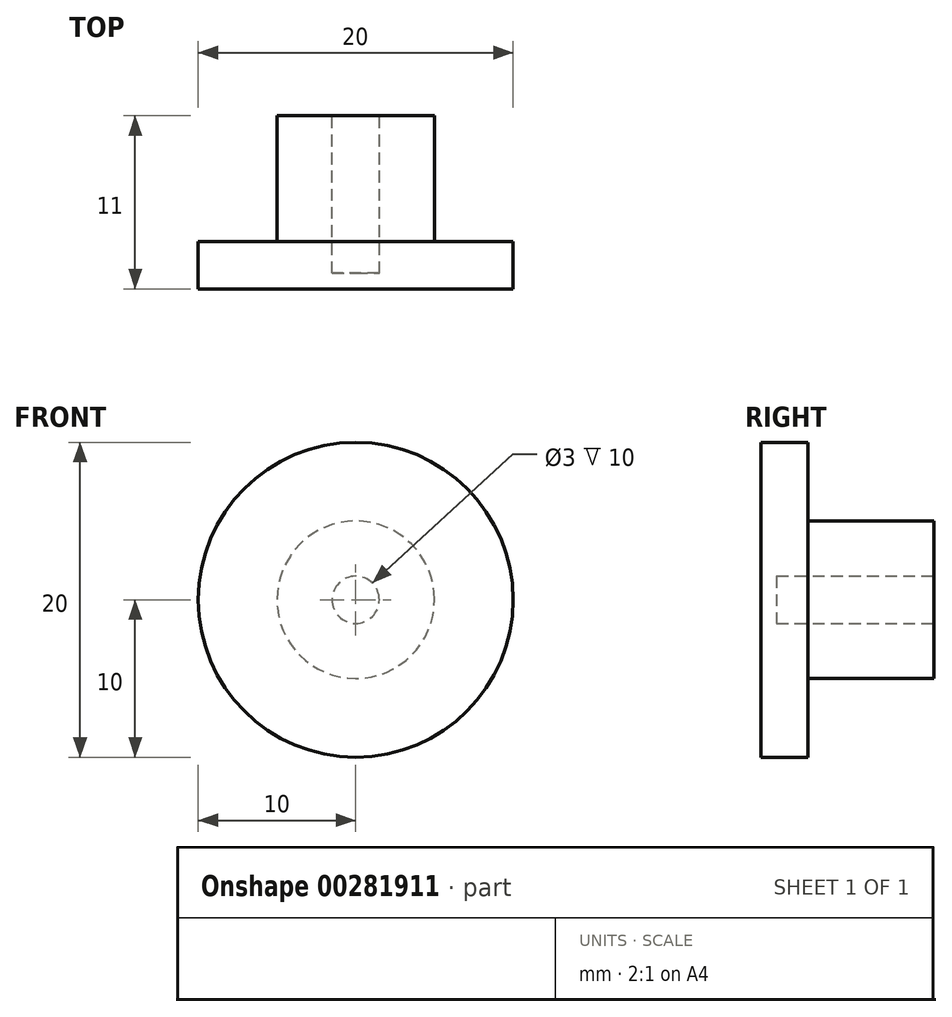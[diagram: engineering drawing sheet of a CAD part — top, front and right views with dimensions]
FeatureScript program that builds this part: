
annotation { "Feature Type Name" : "Feature", "Feature Type Description" : "" }
export const myFeature = defineFeature(function(context is Context, id is Id, definition is map)
    precondition{}
    {
        {
            var Q0;
            Q0=qCreatedBy(makeId("Front.planeOp"),FACE);
            var sketch = newSketch(context, id + "F0", { "sketchPlane" : qUnion([Q0])});
            skCircle(sketch, "E0", {"center": v(0, 0) * mm, "radius": 5 * mm});
            skSolve(sketch);
        }
        {
            var Q0;
            Q0=qSketchRegion(id+"F0",true);
            extrude(context, id + "F1", {"entities" : qUnion([Q0]), "depth" : 8 * mm});
        }
        {
            var Q0;
            Q0=makeQuery(id+"F1.opExtrude","CAP_FACE",FACE,{"disambiguationData":[OSD([sQuery(id+"F0.wireOp",EDGE,"E0")])],"isStart":false});
            var sketch = newSketch(context, id + "F2", { "sketchPlane" : qUnion([Q0])});
            skCircle(sketch, "E1", {"center": v(0, 0) * mm, "radius": 10 * mm});
            skSolve(sketch);
        }
        {
            var Q0;
            Q0=qSketchRegion(id+"F2",true);
            extrude(context, id + "F3", {"entities" : qUnion([Q0]), "operationType" : NewBodyOperationType.ADD, "depth" : 3 * mm});
        }
        {
            var Q0;
            Q0=makeQuery(id+"F1.opExtrude","CAP_FACE",FACE,{"disambiguationData":[OSD([sQuery(id+"F0.wireOp",EDGE,"E0")])],"isStart":true});
            var sketch = newSketch(context, id + "F4", { "sketchPlane" : qUnion([Q0])});
            skCircle(sketch, "E2", {"center": v(0, 0) * mm, "radius": 1.5 * mm});
            skSolve(sketch);
        }
        {
            var Q0;
            Q0=qSketchRegion(id+"F4",true);
            extrude(context, id + "F5", {"entities" : qUnion([Q0]), "operationType" : NewBodyOperationType.REMOVE, "oppositeDirection" : true, "depth" : 10 * mm});
        }
    });
